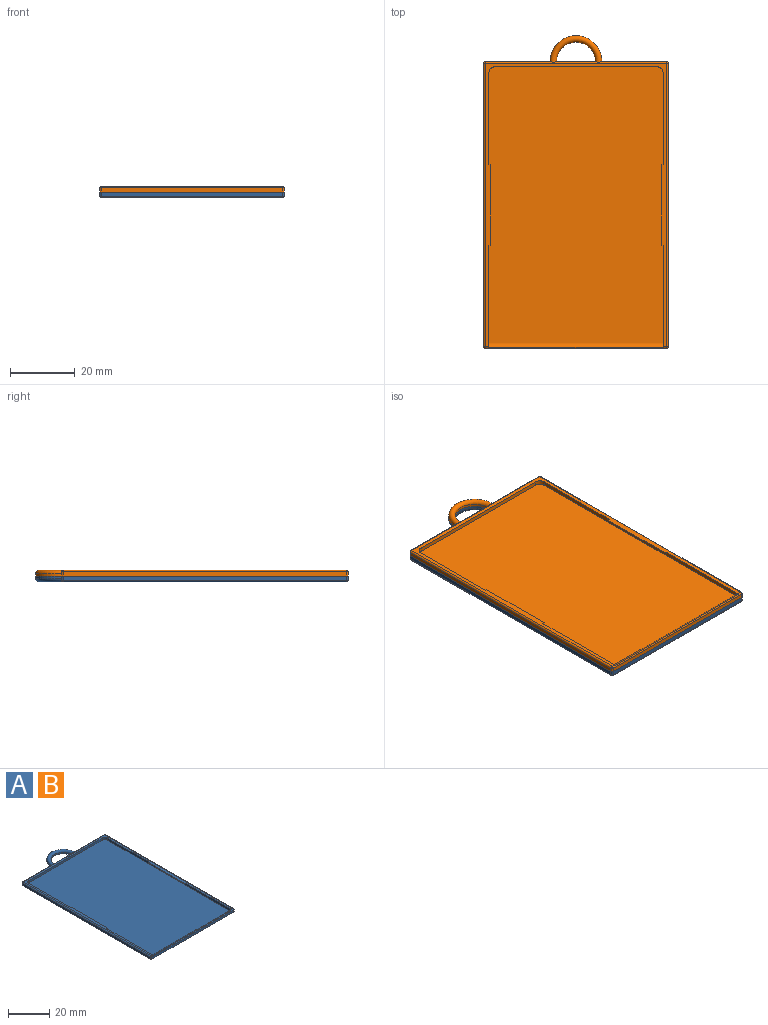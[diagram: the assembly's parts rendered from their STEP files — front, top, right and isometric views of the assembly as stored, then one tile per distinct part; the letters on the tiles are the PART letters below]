
ASSEMBLY  parts=2 mates=1
PART A: 38 faces, bbox 57.2x97.5x1.8 mm
  f0: plane 84.95x1.26mm, normal (1,0,0), area 93.5mm2, adj f12,f13,f14,f15,f18,f21,f22,f34
  f1: plane 96.8x57.18mm, normal (0,0,-1), area 5121.4mm2, adj f4,f5,f6,f7,f8,f9,f10,f11
  f2: plane 84.95x1.26mm, normal (-1,0,0), area 93.5mm2, adj f12,f13,f16,f17,f19,f20,f22,f34
  f3: plane 49.98x1.26mm, normal (0,-1,0), area 63mm2, adj f12,f13,f18,f19
  f4: plane 20.22x1.26mm, normal (0,1,0), area 25.3mm2, adj f1,f5,f23,f24,f37
  f5: cylinder r=8mm len=16mm, axis (0,0,-1), area 19.1mm2, adj f1,f4,f6,f37
  f6: plane 20.22x1.26mm, normal (0,1,0), area 25.3mm2, adj f1,f5,f26,f27,f37
  f7: plane 87.8x1.26mm, normal (-1,0,0), area 110.6mm2, adj f1,f26,f32,f33
  f8: plane 56.18x1.26mm, normal (0,-1,0), area 70.8mm2, adj f1,f29,f32,f34
  f9: cylinder r=6mm len=12mm, axis (0,0,-1), area 14.3mm2, adj f1,f11,f37
  f10: plane 87.8x1.26mm, normal (1,0,0), area 110.6mm2, adj f1,f24,f28,f29
  f11: plane 12.27x1.26mm, normal (0,1,0), area 15.2mm2, adj f1,f9,f36,f37
  f12: plane 87.8x56.18mm, normal (0,0,1), area 279.3mm2, adj f0,f2,f3,f14,f15,f16,f17,f18
  f13: plane 85.6x53.98mm, normal (0,0,1), area 4619mm2, adj f0,f2,f3,f18,f19,f22
  f14: plane 0.5x0.5mm, normal (0,-1,0), area 0.1mm2, adj f0,f12,f21
  f15: plane 0.5x0.5mm, normal (0,1,0), area 0.1mm2, adj f0,f12,f21
  f16: plane 0.5x0.5mm, normal (0,1,0), area 0.1mm2, adj f2,f12,f20
  f17: plane 0.5x0.5mm, normal (0,-1,0), area 0.1mm2, adj f2,f12,f20
  f18: cylinder r=2mm len=2mm, axis (0,0,1), area 4mm2, adj f0,f3,f12,f13
  f19: cylinder r=2mm len=2mm, axis (0,0,-1), area 4mm2, adj f2,f3,f12,f13
  f20: plane 25x0.5mm, normal (-0.71,0,-0.71), area 17.7mm2, adj f2,f12,f16,f17
  f21: plane 25x0.5mm, normal (0.71,0,-0.71), area 17.7mm2, adj f0,f12,f14,f15
  f22: cylinder r=2mm len=53.98mm, axis (-1,0,0), area 100.8mm2, adj f0,f2,f13,f34
  f23: cylinder r=0.5mm len=21.11mm, axis (1,0,0), area 16.2mm2, adj f4,f12,f25,f37
  f24: cylinder r=0.5mm len=1.26mm, axis (0,0,-1), area 1mm2, adj f1,f4,f10,f25
  f25: sphere r=0.5mm, area 0.4mm2, adj f23,f24,f28
  f26: cylinder r=0.5mm len=1.26mm, axis (0,0,1), area 1mm2, adj f1,f6,f7,f30
  f27: cylinder r=0.5mm len=21.11mm, axis (1,0,0), area 16.2mm2, adj f6,f12,f30,f37
  f28: cylinder r=0.5mm len=87.8mm, axis (0,-1,0), area 69mm2, adj f10,f12,f25,f31
  f29: cylinder r=0.5mm len=1.26mm, axis (0,0,1), area 1mm2, adj f1,f8,f10,f31
  f30: sphere r=0.5mm, area 0.4mm2, adj f26,f27,f33
  f31: sphere r=0.5mm, area 0.4mm2, adj f28,f29,f34
  f32: cylinder r=0.5mm len=1.26mm, axis (0,0,-1), area 1mm2, adj f1,f7,f8,f35
  f33: cylinder r=0.5mm len=87.8mm, axis (0,1,0), area 69mm2, adj f7,f12,f30,f35
  f34: cylinder r=0.5mm len=56.18mm, axis (-1,0,0), area 30.1mm2, adj f0,f2,f8,f12,f22,f31,f35
  f35: sphere r=0.5mm, area 0.4mm2, adj f32,f33,f34
  f36: cylinder r=0.5mm len=13.96mm, axis (1,0,0), area 10.2mm2, adj f11,f12,f37
  f37: torus R=7mm, axis (0,0,1), area 69.9mm2, adj f4,f5,f6,f9,f11,f23,f27,f36
PART B: same geometry as A
PLACE A rot(axis=(0,1,0),180deg) t=(-44.71,-13.24,23.7)mm
PLACE B t=(-44.71,-13.24,23.7)mm
MATE fastened A.f1 <-> B.f1  axis (0,0,1) through (-44.71,-12.82,23.7)mm
